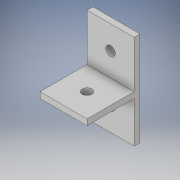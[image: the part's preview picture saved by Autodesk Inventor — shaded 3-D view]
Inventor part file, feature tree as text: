
AUTODESK INVENTOR PART (.ipt)
format: ipt  version: 2018 (Build 220112000, 112)  size: 118,272 bytes
history: native  units: in
note: dims shown in document units (in); Inventor stores cm internally (conversion verified against a paired STEP export)
features: sketch x2, extrude x2, plane x1
ambient origin geometry x8: Origin, YZ Plane, XZ Plane, XY Plane, X Axis, Y Axis, Z Axis, Center Point
bodies: Solid1 (feature_tree)
feature tree (5):
  sketch  "Sketch1"  dims[d0=1.0in d1=2.0in]
  plane  "Work Plane1"
  extrude  "Extrusion3"  Depth=2.0in
  extrude  "Extrusion4"  Depth=1.0in
  sketch  "Sketch2"  dims[d5=1.0in d6=1.0in d9=0.5in d10=0.2031in d11=0.125in d12=0.0in d13=0.5in d14=0.2031in d15=0.5in d16=0.2031in d17=0.125in d18=0.0in]
